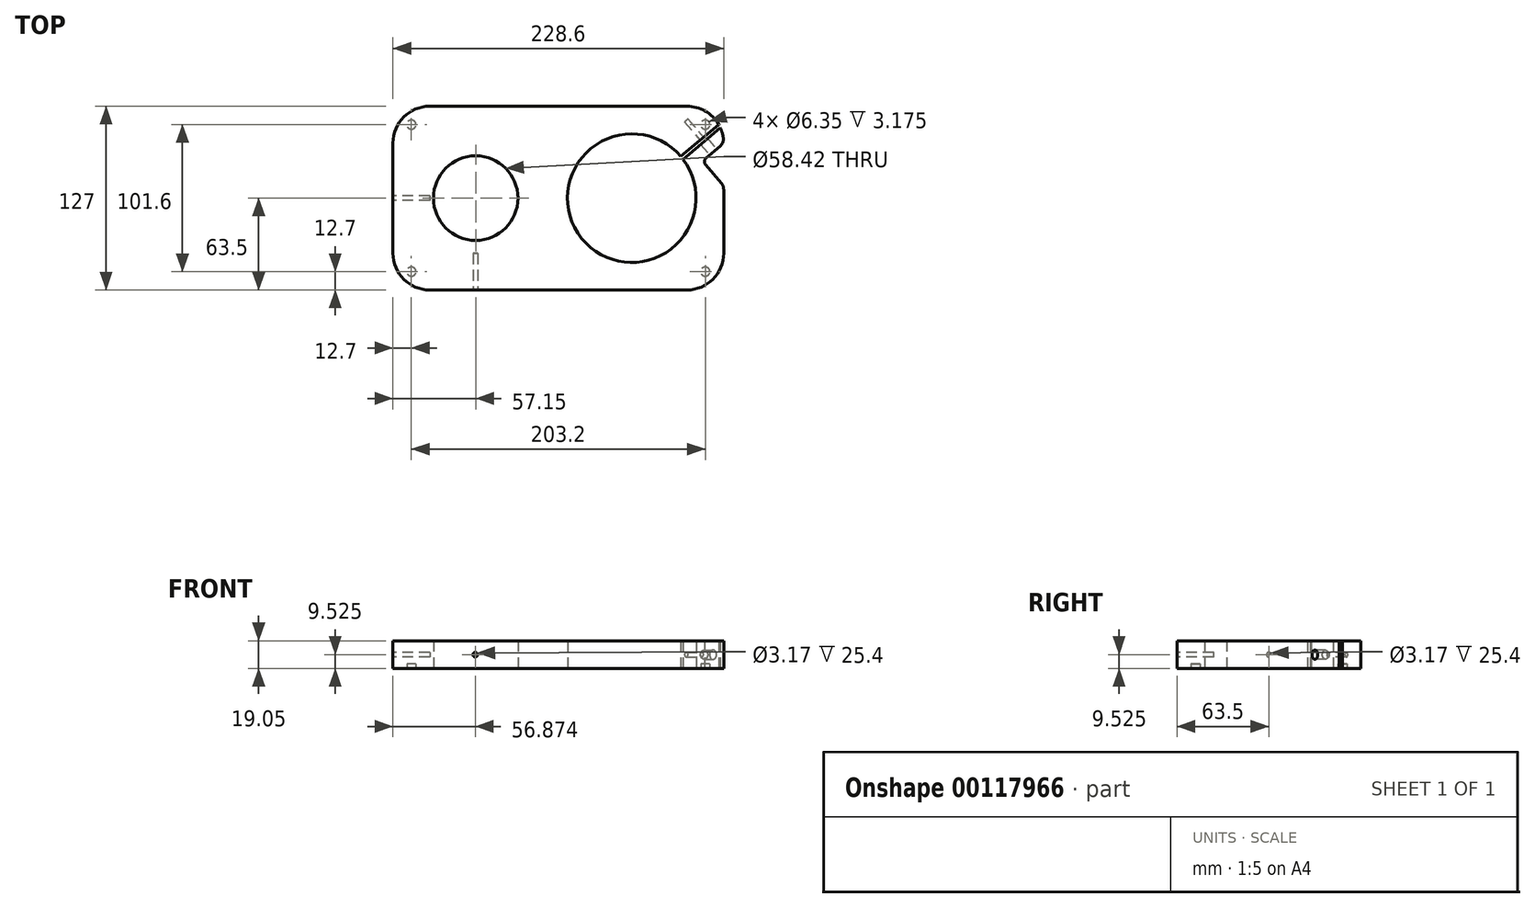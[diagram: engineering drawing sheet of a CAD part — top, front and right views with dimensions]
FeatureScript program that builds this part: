
annotation { "Feature Type Name" : "Feature", "Feature Type Description" : "" }
export const myFeature = defineFeature(function(context is Context, id is Id, definition is map)
    precondition{}
    {
        {
            var Q0;
            Q0=qCreatedBy(makeId("Top.planeOp"),FACE);
            var sketch = newSketch(context, id + "F0", { "sketchPlane" : qUnion([Q0])});
            skLineSegment(sketch, "E0.bottom", {"start": v(-139.7, 63.5) * mm, "end": v(38.1, 63.5) * mm});
            skLineSegment(sketch, "E0.top", {"start": v(-139.7, -63.5) * mm, "end": v(38.1, -63.5) * mm});
            skLineSegment(sketch, "E0.left", {"start": v(-165.1, 38.1) * mm, "end": v(-165.1, -38.1) * mm});
            skArc(sketch, "E1.filletArc", {"start": v(-139.7, 63.5) * mm, "mid": v(-157.66, 56.06) * mm, "end": v(-165.1, 38.1) * mm});
            skArc(sketch, "E2.filletArc", {"start": v(-165.1, -38.1) * mm, "mid": v(-157.66, -56.06) * mm, "end": v(-139.7, -63.5) * mm});
            skCircle(sketch, "E3", {"center": v(-107.95, 0) * mm, "radius": 29.21 * mm});
            skLineSegment(sketch, "E4", {"start": v(63.5, 7.26) * mm, "end": v(63.5, 7.15) * mm});
            skArc(sketch, "E5.filletArc", {"start": v(63.23, 41.79) * mm, "mid": v(62.46, 45.3) * mm, "end": v(61.2, 48.65) * mm});
            skArc(sketch, "E6.filletArc", {"start": v(38.1, -63.5) * mm, "mid": v(56.06, -56.06) * mm, "end": v(63.5, -38.1) * mm});
            skLineSegment(sketch, "E7", {"start": v(-226.7, 50.8) * mm, "end": v(140.03, 50.8) * mm, "construction": true});
            skLineSegment(sketch, "E8", {"start": v(-224.1, -50.8) * mm, "end": v(141.89, -50.8) * mm, "construction": true});
            skLineSegment(sketch, "E9", {"start": v(-152.4, 90.06) * mm, "end": v(-152.4, -83.18) * mm, "construction": true});
            skLineSegment(sketch, "E10", {"start": v(50.8, 89.73) * mm, "end": v(50.8, -84.09) * mm, "construction": true});
            skCircle(sketch, "E11", {"center": v(-152.4, 50.8) * mm, "radius": 3.18 * mm, "construction": true});
            skCircle(sketch, "E12", {"center": v(50.8, 50.8) * mm, "radius": 3.18 * mm, "construction": true});
            skCircle(sketch, "E13", {"center": v(50.8, -50.8) * mm, "radius": 3.18 * mm, "construction": true});
            skCircle(sketch, "E14", {"center": v(-152.4, -50.8) * mm, "radius": 3.18 * mm, "construction": true});
            skLineSegment(sketch, "E15", {"start": v(-227.14, 0) * mm, "end": v(139.66, 0) * mm, "construction": true});
            skLineSegment(sketch, "E16.trimOffspring", {"start": v(63.5, 6.14) * mm, "end": v(63.5, -38.1) * mm});
            skLineSegment(sketch, "E17", {"start": v(0, 0) * mm, "end": v(65.9, 55.96) * mm, "construction": true});
            skArc(sketch, "E18", {"start": v(33.88, 28.77) * mm, "mid": v(-34.69, -27.8) * mm, "end": v(35.47, 26.8) * mm});
            skLineSegment(sketch, "E19", {"start": v(67.9, 54.34) * mm, "end": v(35.47, 26.8) * mm, "construction": true});
            skLineSegment(sketch, "E20", {"start": v(60, 50.96) * mm, "end": v(33.88, 28.77) * mm});
            skLineSegment(sketch, "E21", {"start": v(35.47, 26.8) * mm, "end": v(63.74, 50.8) * mm});
            skLineSegment(sketch, "E22", {"start": v(61.06, 36.03) * mm, "end": v(51.3, 27.74) * mm});
            skLineSegment(sketch, "E23", {"start": v(50.94, 23.27) * mm, "end": v(62, 10.25) * mm});
            skArc(sketch, "E24.trimOffspring", {"start": v(60, 50.96) * mm, "mid": v(50.72, 60.14) * mm, "end": v(38.1, 63.5) * mm});
            skPoint(sketch, "E25.visualSharp", {"position": v(48.88, 25.69) * mm});
            skArc(sketch, "E25.filletArc", {"start": v(51.3, 27.74) * mm, "mid": v(50.2, 25.58) * mm, "end": v(50.94, 23.27) * mm});
            skArc(sketch, "E26.filletArc", {"start": v(63.5, 6.14) * mm, "mid": v(63.11, 8.33) * mm, "end": v(62, 10.25) * mm});
            skPoint(sketch, "E27.visualSharp", {"position": v(63.5, 38.1) * mm});
            skArc(sketch, "E27.filletArc", {"start": v(61.06, 36.03) * mm, "mid": v(62.89, 38.63) * mm, "end": v(63.23, 41.79) * mm});
            skLineSegment(sketch, "E28", {"start": v(-50.8, 88.22) * mm, "end": v(-50.8, -85.44) * mm, "construction": true});
            skLineSegment(sketch, "E29", {"start": v(-63.5, 86.4) * mm, "end": v(-63.5, -85.21) * mm, "construction": true});
            skCircle(sketch, "E30.MirrorC", {"center": v(-83.64, 29.9) * mm, "radius": 15.88 * mm, "construction": true});
            skCircle(sketch, "E31.MirrorC", {"center": v(-83.64, -29.9) * mm, "radius": 15.88 * mm, "construction": true});
            skSolve(sketch);
        }
        {
            var Q0;
            Q0 = qSketchRegion(id + "F0", true);
            extrude(context, id + "F10", {"entities" : qUnion([Q0]), "depth" : 19.05 * mm});
        }
        {
            var Q0;
            Q0=makeQuery(id+"F0.imprint","IMPRINT",FACE,{"disambiguationData":[TD([[makeQuery(id+"F0.imprint","IMPRINT",EDGE,{"derivedFrom":sQuery(id+"F0.wireOp",EDGE,"E0.bottom")}),-1.0]])]});
            var sketch = newSketch(context, id + "F1", { "sketchPlane" : qUnion([Q0])});
            skCircle(sketch, "E32", {"center": v(-152.4, -50.8) * mm, "radius": 3.18 * mm});
            skCircle(sketch, "E33", {"center": v(50.8, -50.8) * mm, "radius": 3.18 * mm});
            skCircle(sketch, "E34", {"center": v(50.8, 50.8) * mm, "radius": 3.18 * mm});
            skCircle(sketch, "E35", {"center": v(-152.4, 50.8) * mm, "radius": 3.18 * mm});
            skSolve(sketch);
        }
        {
            var Q0;
            Q0 = qSketchRegion(id + "F1", true);
            extrude(context, id + "F2", {"entities" : qUnion([Q0]), "operationType" : NewBodyOperationType.REMOVE, "depth" : 3.17 * mm});
        }
        {
            var Q0;
            Q0=makeQuery(id+"F10.opExtrude","SWEPT_FACE",FACE,{"disambiguationData":[OSD([sQuery(id+"F0.wireOp",EDGE,"E22")])]});
            var sketch = newSketch(context, id + "F3", { "sketchPlane" : qUnion([Q0])});
            skCircle(sketch, "E36", {"center": v(63.46, 9.53) * mm, "radius": 1.59 * mm});
            skLineSegment(sketch, "E37", {"start": v(69.86, 19.05) * mm, "end": v(57.06, 0) * mm, "construction": true});
            skLineSegment(sketch, "E38", {"start": v(57.06, 19.05) * mm, "end": v(69.86, 0) * mm, "construction": true});
            skSolve(sketch);
        }
        {
            var Q0;
            Q0 = qSketchRegion(id + "F3", true);
            extrude(context, id + "F4", {"entities" : qUnion([Q0]), "operationType" : NewBodyOperationType.REMOVE, "oppositeDirection" : true, "depth" : 28.57 * mm});
        }
        {
            var Q0;
            Q0=makeQuery(id+"F3.imprint","IMPRINT",FACE,{"disambiguationData":[TD([[makeQuery(id+"F3.imprint","IMPRINT",EDGE,{"derivedFrom":sQuery(id+"F3.wireOp",EDGE,"E36")}),-1.0]])]});
            var sketch = newSketch(context, id + "F5", { "sketchPlane" : qUnion([Q0])});
            skCircle(sketch, "E39", {"center": v(63.46, 9.53) * mm, "radius": 3.17 * mm});
            skSolve(sketch);
        }
        {
            var Q0;
            Q0 = qSketchRegion(id + "F5", true);
            extrude(context, id + "F11", {"entities" : qUnion([Q0]), "operationType" : NewBodyOperationType.REMOVE, "endBound" : BoundingType.UP_TO_NEXT, "oppositeDirection" : true, "depth" : 25.4 * mm});
        }
        {
            var Q0;
            Q0=makeQuery(id+"F10.opExtrude","SWEPT_FACE",FACE,{"disambiguationData":[OSD([sQuery(id+"F0.wireOp",EDGE,"E0.top")])]});
            var sketch = newSketch(context, id + "F6", { "sketchPlane" : qUnion([Q0])});
            skCircle(sketch, "E40", {"center": v(-108.23, 9.53) * mm, "radius": 1.59 * mm});
            skLineSegment(sketch, "E41", {"start": v(-108.23, 19.05) * mm, "end": v(-108.23, 0) * mm, "construction": true});
            skSolve(sketch);
        }
        {
            var Q0;
            Q0=makeQuery(id+"F6.imprint","IMPRINT",FACE,{"disambiguationData":[TD([[makeQuery(id+"F6.imprint","IMPRINT",EDGE,{"derivedFrom":sQuery(id+"F6.wireOp",EDGE,"E40")}),1.0]])]});
            var Q1;
            Q1=sQuery(id+"F6.wireOp",EDGE,"E40");
            extrude(context, id + "F7", {"entities" : qUnion([Q0]), "operationType" : NewBodyOperationType.REMOVE, "surfaceEntities" : qUnion([Q1]), "oppositeDirection" : true, "depth" : 25.4 * mm});
        }
        {
            var Q0;
            Q0=makeQuery(id+"F10.opExtrude","SWEPT_FACE",FACE,{"disambiguationData":[OSD([sQuery(id+"F0.wireOp",EDGE,"E0.left")])]});
            var sketch = newSketch(context, id + "F8", { "sketchPlane" : qUnion([Q0])});
            skLineSegment(sketch, "E42", {"start": v(0, 19.05) * mm, "end": v(0, 0) * mm, "construction": true});
            skCircle(sketch, "E43", {"center": v(0, 9.53) * mm, "radius": 1.59 * mm});
            skSolve(sketch);
        }
        {
            var Q0;
            Q0=makeQuery(id+"F8.imprint","IMPRINT",FACE,{"disambiguationData":[TD([[makeQuery(id+"F8.imprint","IMPRINT",EDGE,{"derivedFrom":sQuery(id+"F8.wireOp",EDGE,"E43")}),1.0]])]});
            var Q1;
            Q1=sQuery(id+"F8.wireOp",EDGE,"E43");
            extrude(context, id + "F9", {"entities" : qUnion([Q0]), "operationType" : NewBodyOperationType.REMOVE, "surfaceEntities" : qUnion([Q1]), "oppositeDirection" : true, "depth" : 25.4 * mm});
        }
    });
